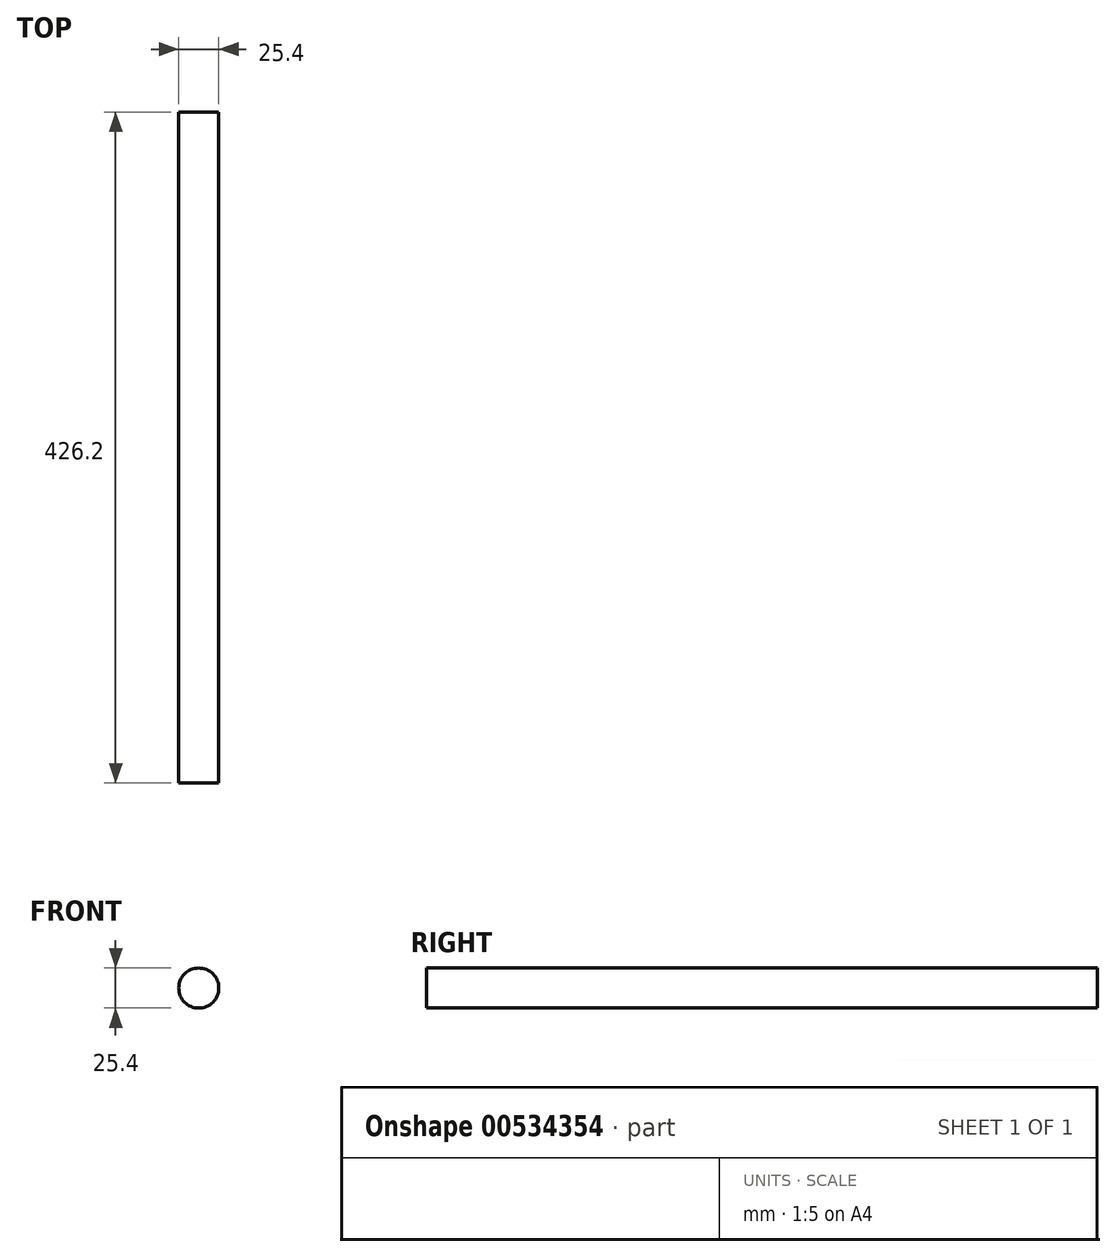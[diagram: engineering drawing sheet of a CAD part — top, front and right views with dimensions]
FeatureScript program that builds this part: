
annotation { "Feature Type Name" : "Feature", "Feature Type Description" : "" }
export const myFeature = defineFeature(function(context is Context, id is Id, definition is map)
    precondition{}
    {
        {
            var Q0;
            Q0=qCreatedBy(makeId("Front.planeOp"),FACE);
            var sketch = newSketch(context, id + "F0", { "sketchPlane" : qUnion([Q0])});
            skCircle(sketch, "E0", {"center": v(0, 0) * mm, "radius": 12.7 * mm});
            skSolve(sketch);
        }
        {
            var Q0;
            Q0=makeQuery(id+"F0.imprint","IMPRINT",FACE,{"disambiguationData":[TD([[makeQuery(id+"F0.imprint","IMPRINT",EDGE,{"derivedFrom":sQuery(id+"F0.wireOp",EDGE,"E0")}),1.0]])]});
            extrude(context, id + "F1", {"entities" : qUnion([Q0]), "depth" : (407.15 + 19.05) * mm, "offsetDistance" : 25 * mm});
        }
    });
